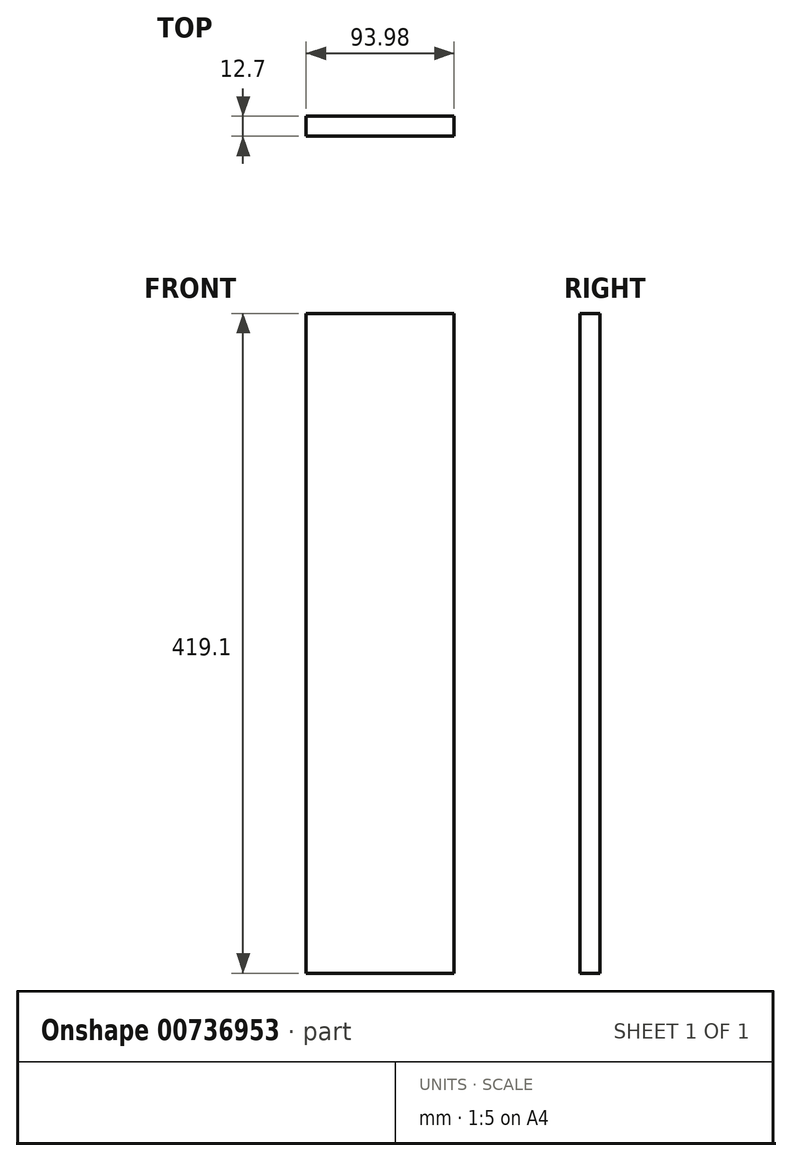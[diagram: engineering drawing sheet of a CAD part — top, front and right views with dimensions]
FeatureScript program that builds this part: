
annotation { "Feature Type Name" : "Feature", "Feature Type Description" : "" }
export const myFeature = defineFeature(function(context is Context, id is Id, definition is map)
    precondition{}
    {
        {
            var Q0;
            Q0=qCreatedBy(makeId("Front.planeOp"),FACE);
            var sketch = newSketch(context, id + "F0", { "sketchPlane" : qUnion([Q0])});
            skLineSegment(sketch, "E0.bottom", {"start": v(-46.99, 209.55) * mm, "end": v(47, 209.55) * mm});
            skLineSegment(sketch, "E0.top", {"start": v(-47, -209.55) * mm, "end": v(46.99, -209.55) * mm});
            skLineSegment(sketch, "E0.left", {"start": v(-46.99, 209.55) * mm, "end": v(-47, -209.55) * mm});
            skLineSegment(sketch, "E0.right", {"start": v(47, 209.55) * mm, "end": v(46.99, -209.55) * mm});
            skPoint(sketch, "E0.middle", {"position": v(0, 0) * mm});
            skSolve(sketch);
        }
        {
            var Q0;
            Q0=qSketchRegion(id+"F0",true);
            extrude(context, id + "F1", {"entities" : qUnion([Q0]), "depth" : 12.7 * mm, "offsetDistance" : 25.4 * mm});
        }
    });
